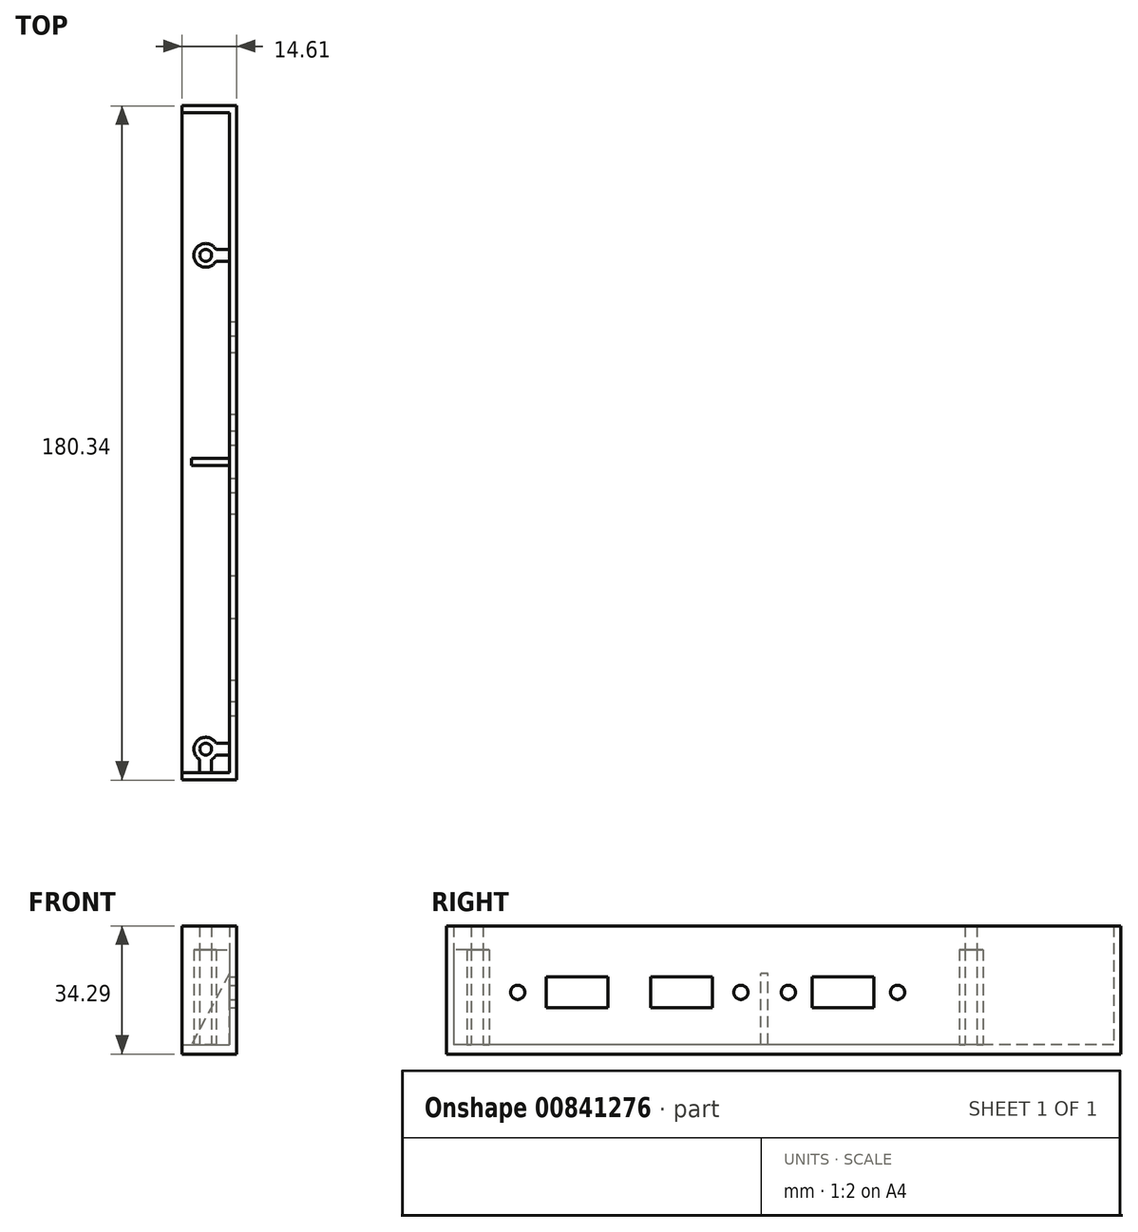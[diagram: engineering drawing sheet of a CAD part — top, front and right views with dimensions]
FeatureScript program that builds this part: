
annotation { "Feature Type Name" : "Feature", "Feature Type Description" : "" }
export const myFeature = defineFeature(function(context is Context, id is Id, definition is map)
    precondition{}
    {
        {
            var Q0;
            Q0=qCreatedBy(makeId("Top.planeOp"),FACE);
            var sketch = newSketch(context, id + "F0", { "sketchPlane" : qUnion([Q0])});
            skCircle(sketch, "E0", {"center": v(0, 132.08) * mm, "radius": 3.18 * mm});
            skCircle(sketch, "E1", {"center": v(0, 0) * mm, "radius": 3.18 * mm});
            skCircle(sketch, "E2", {"center": v(0, 132.08) * mm, "radius": 1.59 * mm});
            skCircle(sketch, "E3", {"center": v(0, 0) * mm, "radius": 1.59 * mm});
            skLineSegment(sketch, "E4", {"start": v(0, 132.08) * mm, "end": v(0, 0) * mm, "construction": true});
            skLineSegment(sketch, "E5", {"start": v(0, 170.18) * mm, "end": v(6.35, 170.18) * mm});
            skLineSegment(sketch, "E6", {"start": v(6.35, 170.18) * mm, "end": v(6.35, -6.35) * mm});
            skLineSegment(sketch, "E7", {"start": v(6.35, -6.35) * mm, "end": v(0, -6.35) * mm});
            skLineSegment(sketch, "E8.MirrorCS", {"start": v(-6.35, -6.35) * mm, "end": v(0, -6.35) * mm});
            skLineSegment(sketch, "E9.MirrorCS", {"start": v(0, 170.18) * mm, "end": v(-6.35, 170.18) * mm});
            skLineSegment(sketch, "E10.MirrorCS", {"start": v(-6.35, 170.18) * mm, "end": v(-6.35, -6.35) * mm});
            skSolve(sketch);
        }
        {
            var Q0;
            Q0=makeQuery(id+"F0.imprint","IMPRINT",FACE,{"disambiguationData":[TD([[makeQuery(id+"F0.imprint","IMPRINT",EDGE,{"derivedFrom":sQuery(id+"F0.wireOp",EDGE,"E0")}),-1.0]])]});
            var Q1;
            Q1=makeQuery(id+"F0.imprint","IMPRINT",FACE,{"disambiguationData":[TD([[makeQuery(id+"F0.imprint","IMPRINT",EDGE,{"derivedFrom":sQuery(id+"F0.wireOp",EDGE,"E0")}),1.0]])]});
            var Q2;
            Q2=makeQuery(id+"F0.imprint","IMPRINT",FACE,{"disambiguationData":[TD([[makeQuery(id+"F0.imprint","IMPRINT",EDGE,{"derivedFrom":sQuery(id+"F0.wireOp",EDGE,"E2")}),1.0]])]});
            var Q3;
            Q3=makeQuery(id+"F0.imprint","IMPRINT",FACE,{"disambiguationData":[TD([[makeQuery(id+"F0.imprint","IMPRINT",EDGE,{"derivedFrom":sQuery(id+"F0.wireOp",EDGE,"E1")}),1.0]])]});
            var Q4;
            Q4=makeQuery(id+"F0.imprint","IMPRINT",FACE,{"disambiguationData":[TD([[makeQuery(id+"F0.imprint","IMPRINT",EDGE,{"derivedFrom":sQuery(id+"F0.wireOp",EDGE,"E3")}),1.0]])]});
            extrude(context, id + "F1", {"entities" : qUnion([Q0, Q1, Q2, Q3, Q4]), "oppositeDirection" : true, "depth" : 2.54 * mm, "offsetDistance" : 25.4 * mm});
        }
        {
            var Q0;
            Q0=makeQuery(id+"F0.imprint","IMPRINT",FACE,{"disambiguationData":[TD([[makeQuery(id+"F0.imprint","IMPRINT",EDGE,{"derivedFrom":sQuery(id+"F0.wireOp",EDGE,"E0")}),1.0]])]});
            var Q1;
            Q1=makeQuery(id+"F0.imprint","IMPRINT",FACE,{"disambiguationData":[TD([[makeQuery(id+"F0.imprint","IMPRINT",EDGE,{"derivedFrom":sQuery(id+"F0.wireOp",EDGE,"E2")}),1.0]])]});
            var Q2;
            Q2=makeQuery(id+"F0.imprint","IMPRINT",FACE,{"disambiguationData":[TD([[makeQuery(id+"F0.imprint","IMPRINT",EDGE,{"derivedFrom":sQuery(id+"F0.wireOp",EDGE,"E3")}),1.0]])]});
            var Q3;
            Q3=makeQuery(id+"F0.imprint","IMPRINT",FACE,{"disambiguationData":[TD([[makeQuery(id+"F0.imprint","IMPRINT",EDGE,{"derivedFrom":sQuery(id+"F0.wireOp",EDGE,"E1")}),1.0]])]});
            extrude(context, id + "F2", {"entities" : qUnion([Q0, Q1, Q2, Q3]), "operationType" : NewBodyOperationType.ADD, "depth" : 25.4 * mm, "offsetDistance" : 25.4 * mm});
        }
        {
            var Q0;
            Q0=makeQuery(id+"F0.imprint","IMPRINT",FACE,{"disambiguationData":[TD([[makeQuery(id+"F0.imprint","IMPRINT",EDGE,{"derivedFrom":sQuery(id+"F0.wireOp",EDGE,"E3")}),1.0]])]});
            var Q1;
            Q1=makeQuery(id+"F0.imprint","IMPRINT",FACE,{"disambiguationData":[TD([[makeQuery(id+"F0.imprint","IMPRINT",EDGE,{"derivedFrom":sQuery(id+"F0.wireOp",EDGE,"E2")}),1.0]])]});
            extrude(context, id + "F3", {"entities" : qUnion([Q0, Q1]), "operationType" : NewBodyOperationType.ADD, "depth" : 31.75 * mm, "offsetDistance" : 25.4 * mm});
        }
        {
            var Q0;
            Q0=qCreatedBy(makeId("Top.planeOp"),FACE);
            var sketch = newSketch(context, id + "F4", { "sketchPlane" : qUnion([Q0])});
            skLineSegment(sketch, "E11.0", {"start": v(-6.35, -8.25) * mm, "end": v(8.26, -8.25) * mm});
            skLineSegment(sketch, "E11.1", {"start": v(8.25, 172.09) * mm, "end": v(8.26, -8.25) * mm});
            skLineSegment(sketch, "E11.2", {"start": v(8.25, 172.09) * mm, "end": v(-6.35, 172.09) * mm});
            skLineSegment(sketch, "E12", {"start": v(-6.35, 172.09) * mm, "end": v(-6.35, 170.18) * mm});
            skLineSegment(sketch, "E13", {"start": v(-6.35, -8.25) * mm, "end": v(-6.35, -6.35) * mm});
            skLineSegment(sketch, "E14.0", {"start": v(6.35, 170.18) * mm, "end": v(-6.35, 170.18) * mm});
            skLineSegment(sketch, "E15.0", {"start": v(6.35, 170.18) * mm, "end": v(6.35, -6.35) * mm});
            skLineSegment(sketch, "E16.0", {"start": v(-6.35, -6.35) * mm, "end": v(6.35, -6.35) * mm});
            skSolve(sketch);
        }
        {
            var Q0;
            Q0 = qSketchRegion(id + "F4", true);
            var Q1;
            Q1=makeQuery(id+"F1.opExtrude","CAP_FACE",FACE,{"disambiguationData":[OSD([sQuery(id+"F0.wireOp",EDGE,"E5"),sQuery(id+"F0.wireOp",EDGE,"E6"),sQuery(id+"F0.wireOp",EDGE,"E7"),sQuery(id+"F0.wireOp",EDGE,"E8.MirrorCS"),sQuery(id+"F0.wireOp",EDGE,"E9.MirrorCS"),sQuery(id+"F0.wireOp",EDGE,"E10.MirrorCS")])],"isStart":false});
            extrude(context, id + "F5", {"entities" : qUnion([Q0]), "operationType" : NewBodyOperationType.ADD, "depth" : 31.75 * mm, "offsetDistance" : 25.4 * mm, "hasSecondDirection" : true, "secondDirectionBound" : SecondDirectionBoundingType.UP_TO_SURFACE, "secondDirectionOppositeDirection" : true, "secondDirectionDepth" : 25.4 * mm, "secondDirectionBoundEntityFace" : qUnion([Q1])});
        }
        {
            var Q0;
            Q0=makeQuery(id+"F1.opExtrude","CAP_FACE",FACE,{"disambiguationData":[OSD([sQuery(id+"F0.wireOp",EDGE,"E5"),sQuery(id+"F0.wireOp",EDGE,"E6"),sQuery(id+"F0.wireOp",EDGE,"E7"),sQuery(id+"F0.wireOp",EDGE,"E8.MirrorCS"),sQuery(id+"F0.wireOp",EDGE,"E9.MirrorCS"),sQuery(id+"F0.wireOp",EDGE,"E10.MirrorCS")])],"isStart":true});
            var sketch = newSketch(context, id + "F6", { "sketchPlane" : qUnion([Q0])});
            skArc(sketch, "E17.0", {"start": v(0, 133.67) * mm, "mid": v(-1.59, 132.08) * mm, "end": v(0, 130.5) * mm});
            skArc(sketch, "E18.0", {"start": v(0, 1.59) * mm, "mid": v(-1.12, 1.12) * mm, "end": v(-1.59, 0) * mm});
            skLineSegment(sketch, "E19", {"start": v(0, 133.67) * mm, "end": v(6.35, 133.67) * mm});
            skLineSegment(sketch, "E20", {"start": v(0, 130.5) * mm, "end": v(6.35, 130.5) * mm});
            skLineSegment(sketch, "E21", {"start": v(6.35, 130.5) * mm, "end": v(6.35, 133.67) * mm});
            skLineSegment(sketch, "E22", {"start": v(0, 1.59) * mm, "end": v(6.35, 1.59) * mm});
            skLineSegment(sketch, "E23", {"start": v(-1.59, 0) * mm, "end": v(-1.59, -6.35) * mm});
            skLineSegment(sketch, "E24", {"start": v(-1.59, -6.35) * mm, "end": v(1.59, -6.35) * mm});
            skLineSegment(sketch, "E25", {"start": v(1.59, -1.59) * mm, "end": v(1.59, -6.35) * mm});
            skLineSegment(sketch, "E26", {"start": v(6.35, 1.59) * mm, "end": v(6.35, 1.59) * mm});
            skLineSegment(sketch, "E27", {"start": v(1.59, -1.59) * mm, "end": v(6.35, -1.59) * mm});
            skLineSegment(sketch, "E28", {"start": v(6.35, -1.59) * mm, "end": v(6.35, 1.59) * mm});
            skPoint(sketch, "E29.orphan", {"position": v(1.59, 0) * mm});
            skPoint(sketch, "E30.orphan", {"position": v(0, -1.59) * mm});
            skSolve(sketch);
        }
        {
            var Q0;
            Q0 = qSketchRegion(id + "F6", true);
            extrude(context, id + "F7", {"entities" : qUnion([Q0]), "operationType" : NewBodyOperationType.ADD, "depth" : 25.4 * mm, "offsetDistance" : 25.4 * mm});
        }
        {
            var Q0;
            Q0=makeQuery(id+"F5.opExtrude","SWEPT_FACE",FACE,{"disambiguationData":[OSD([sQuery(id+"F4.wireOp",EDGE,"E11.1")])]});
            var sketch = newSketch(context, id + "F8", { "sketchPlane" : qUnion([Q0])});
            skLineSegment(sketch, "E31.bottom", {"start": v(2.54, 7.62) * mm, "end": v(127, 7.62) * mm, "construction": true});
            skLineSegment(sketch, "E31.top", {"start": v(2.54, 20.32) * mm, "end": v(127, 20.32) * mm, "construction": true});
            skLineSegment(sketch, "E31.left", {"start": v(2.54, 7.62) * mm, "end": v(2.54, 20.32) * mm, "construction": true});
            skLineSegment(sketch, "E31.right", {"start": v(127, 7.62) * mm, "end": v(127, 20.32) * mm, "construction": true});
            skLineSegment(sketch, "E32", {"start": v(40.64, 20.32) * mm, "end": v(40.64, 7.62) * mm, "construction": true});
            skLineSegment(sketch, "E33.bottom", {"start": v(34.92, 18.1) * mm, "end": v(18.41, 18.1) * mm});
            skLineSegment(sketch, "E33.top", {"start": v(34.92, 9.84) * mm, "end": v(18.41, 9.84) * mm});
            skLineSegment(sketch, "E33.left", {"start": v(34.92, 18.1) * mm, "end": v(34.92, 9.84) * mm});
            skLineSegment(sketch, "E33.right", {"start": v(18.41, 18.1) * mm, "end": v(18.41, 9.84) * mm});
            skPoint(sketch, "E33.middle", {"position": v(26.67, 13.97) * mm});
            skPoint(sketch, "E34", {"position": v(40.64, 13.97) * mm});
            skCircle(sketch, "E35", {"center": v(10.8, 13.97) * mm, "radius": 1.9 * mm});
            skPoint(sketch, "E35.centerSnap0", {"position": v(18.41, 13.97) * mm});
            skLineSegment(sketch, "E36.MirrorCS", {"start": v(46.35, 18.1) * mm, "end": v(46.35, 9.84) * mm});
            skLineSegment(sketch, "E37.MirrorCS", {"start": v(46.35, 18.1) * mm, "end": v(62.86, 18.1) * mm});
            skLineSegment(sketch, "E38.MirrorCS", {"start": v(62.87, 18.1) * mm, "end": v(62.87, 9.84) * mm});
            skPoint(sketch, "E39.MirrorP", {"position": v(62.86, 13.97) * mm});
            skCircle(sketch, "E40.MirrorC", {"center": v(70.48, 13.97) * mm, "radius": 1.9 * mm});
            skPoint(sketch, "E41.MirrorP", {"position": v(54.6, 13.97) * mm});
            skLineSegment(sketch, "E42.MirrorCS", {"start": v(46.35, 9.84) * mm, "end": v(62.86, 9.84) * mm});
            skLineSegment(sketch, "E43", {"start": v(97.8, 20.32) * mm, "end": v(97.8, 7.62) * mm, "construction": true});
            skLineSegment(sketch, "E44.bottom", {"start": v(106.05, 18.1) * mm, "end": v(89.54, 18.1) * mm});
            skLineSegment(sketch, "E44.top", {"start": v(106.05, 9.84) * mm, "end": v(89.54, 9.84) * mm});
            skLineSegment(sketch, "E44.left", {"start": v(106.05, 18.1) * mm, "end": v(106.05, 9.84) * mm});
            skLineSegment(sketch, "E44.right", {"start": v(89.54, 18.1) * mm, "end": v(89.54, 9.84) * mm});
            skPoint(sketch, "E44.middle", {"position": v(97.8, 13.97) * mm});
            skCircle(sketch, "E45", {"center": v(83.19, 13.97) * mm, "radius": 1.9 * mm});
            skCircle(sketch, "E46.MirrorC", {"center": v(112.4, 13.97) * mm, "radius": 1.9 * mm});
            skLineSegment(sketch, "E47", {"start": v(76.84, 20.32) * mm, "end": v(76.84, 7.62) * mm, "construction": true});
            skSolve(sketch);
        }
        {
            var Q0;
            Q0 = qSketchRegion(id + "F8", true);
            extrude(context, id + "F9", {"entities" : qUnion([Q0]), "operationType" : NewBodyOperationType.REMOVE, "endBound" : BoundingType.UP_TO_NEXT, "oppositeDirection" : true, "depth" : 25.4 * mm, "offsetDistance" : 25.4 * mm});
        }
        {
            var Q0;
            Q0=qCreatedBy(makeId("Front.planeOp"),FACE);
            cPlane(context, id + "F10", {"entities" : qUnion([Q0]), "cplaneType" : CPlaneType.OFFSET, "offset" : 76.83 * mm, "oppositeDirection" : true, "width" : 152.4 * mm, "height" : 152.4 * mm});
        }
        {
            var Q0;
            Q0=qCreatedBy(id+"F10.planeOp",FACE);
            var sketch = newSketch(context, id + "F11", { "sketchPlane" : qUnion([Q0])});
            skLineSegment(sketch, "E48", {"start": v(-3.81, 0) * mm, "end": v(6.35, 0) * mm});
            skLineSegment(sketch, "E49", {"start": v(6.35, 0) * mm, "end": v(6.35, 19.05) * mm});
            skLineSegment(sketch, "E50", {"start": v(6.35, 19.05) * mm, "end": v(-3.81, 0) * mm});
            skSolve(sketch);
        }
        {
            var Q0;
            Q0 = qSketchRegion(id + "F11", true);
            extrude(context, id + "F12", {"entities" : qUnion([Q0]), "operationType" : NewBodyOperationType.ADD, "endBound" : BoundingType.SYMMETRIC, "oppositeDirection" : true, "depth" : 1.9 * mm, "offsetDistance" : 25.4 * mm});
        }
    });
